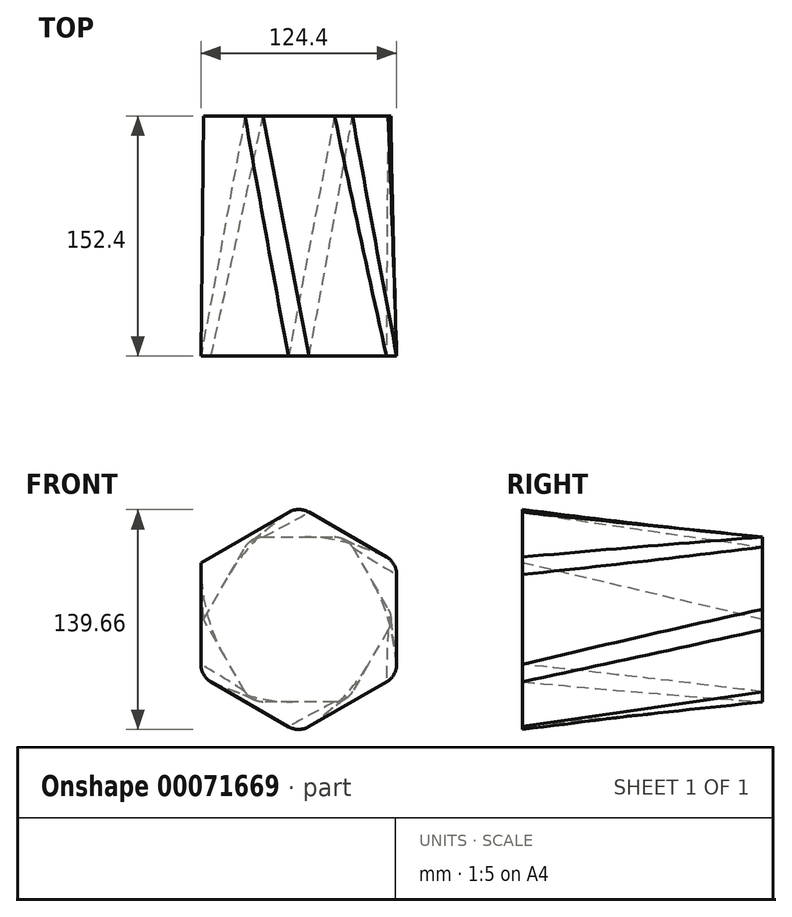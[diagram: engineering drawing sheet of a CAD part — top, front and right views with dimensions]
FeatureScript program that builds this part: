
annotation { "Feature Type Name" : "Feature", "Feature Type Description" : "" }
export const myFeature = defineFeature(function(context is Context, id is Id, definition is map)
    precondition{}
    {
        {
            var Q0;
            Q0=qCreatedBy(makeId("Front.planeOp"),FACE);
            var sketch = newSketch(context, id + "F0", { "sketchPlane" : qUnion([Q0])});
            skCircle(sketch, "E0.cCircle", {"center": v(0, 0) * mm, "radius": 52.46 * mm, "construction": true});
            skLineSegment(sketch, "E0.0", {"start": v(30.29, -52.46) * mm, "end": v(-30.29, -52.46) * mm});
            skLineSegment(sketch, "E0.1", {"start": v(-30.29, -52.46) * mm, "end": v(-60.57, 0) * mm});
            skLineSegment(sketch, "E0.2", {"start": v(-60.57, 0) * mm, "end": v(-30.29, 52.46) * mm});
            skLineSegment(sketch, "E0.3", {"start": v(-30.29, 52.46) * mm, "end": v(30.29, 52.46) * mm});
            skLineSegment(sketch, "E0.4", {"start": v(30.29, 52.46) * mm, "end": v(60.57, 0) * mm});
            skLineSegment(sketch, "E0.5", {"start": v(60.57, 0) * mm, "end": v(30.29, -52.46) * mm});
            skPoint(sketch, "E0.0.midPoint", {"position": v(0, -52.46) * mm});
            skSolve(sketch);
        }
        {
            var Q0;
            Q0=qCreatedBy(makeId("Front.planeOp"),FACE);
            cPlane(context, id + "F1", {"entities" : qUnion([Q0]), "cplaneType" : CPlaneType.OFFSET, "offset" : 152.4 * mm, "width" : 152.4 * mm, "height" : 152.4 * mm});
        }
        {
            var Q0;
            Q0=qCreatedBy(id+"F1.planeOp",FACE);
            var sketch = newSketch(context, id + "F2", { "sketchPlane" : qUnion([Q0])});
            skCircle(sketch, "E1.cCircle", {"center": v(0, 0) * mm, "radius": 62.2 * mm, "construction": true});
            skLineSegment(sketch, "E1.0", {"start": v(-62.2, -35.91) * mm, "end": v(-62.2, 35.91) * mm});
            skLineSegment(sketch, "E1.1", {"start": v(-62.2, 35.91) * mm, "end": v(0, 71.82) * mm});
            skLineSegment(sketch, "E1.2", {"start": v(0, 71.82) * mm, "end": v(62.2, 35.91) * mm});
            skLineSegment(sketch, "E1.3", {"start": v(62.2, 35.91) * mm, "end": v(62.2, -35.91) * mm});
            skLineSegment(sketch, "E1.4", {"start": v(62.2, -35.91) * mm, "end": v(0, -71.82) * mm});
            skLineSegment(sketch, "E1.5", {"start": v(0, -71.82) * mm, "end": v(-62.2, -35.91) * mm});
            skPoint(sketch, "E1.0.midPoint", {"position": v(-62.2, 0) * mm});
            skSolve(sketch);
        }
        {
            var Q0;
            Q0=makeQuery(id+"F0.imprint","IMPRINT",FACE,{"disambiguationData":[TD([[makeQuery(id+"F0.imprint","IMPRINT",EDGE,{"derivedFrom":sQuery(id+"F0.wireOp",EDGE,"E0.0")}),-1.0]])]});
            var Q1;
            Q1=makeQuery(id+"F2.imprint","IMPRINT",FACE,{"disambiguationData":[TD([[makeQuery(id+"F2.imprint","IMPRINT",EDGE,{"derivedFrom":sQuery(id+"F2.wireOp",EDGE,"E1.0")}),-1.0]])]});
            loft(context, id + "F3", {"sheetProfilesArray" : [{ "sheetProfileEntities" : qUnion([Q0]) }, { "sheetProfileEntities" : qUnion([Q1]) }]});
        }
        {
            var Q0;
            Q0=makeQuery(id+"F3.opLoft","SWEPT_EDGE",EDGE,{"disambiguationData":[OSD([sQuery(id+"F0.wireOp",EDGE,"E0.2"),sQuery(id+"F0.wireOp",EDGE,"E0.3"),sQuery(id+"F2.wireOp",EDGE,"E1.1"),sQuery(id+"F2.wireOp",EDGE,"E1.2")])]});
            var Q1;
            Q1=makeQuery(id+"F3.opLoft","SWEPT_EDGE",EDGE,{"disambiguationData":[OSD([sQuery(id+"F0.wireOp",EDGE,"E0.3"),sQuery(id+"F0.wireOp",EDGE,"E0.4"),sQuery(id+"F2.wireOp",EDGE,"E1.2"),sQuery(id+"F2.wireOp",EDGE,"E1.3")])]});
            var Q2;
            Q2=makeQuery(id+"F3.opLoft","SWEPT_EDGE",EDGE,{"disambiguationData":[OSD([sQuery(id+"F0.wireOp",EDGE,"E0.4"),sQuery(id+"F0.wireOp",EDGE,"E0.5"),sQuery(id+"F2.wireOp",EDGE,"E1.3"),sQuery(id+"F2.wireOp",EDGE,"E1.4")])]});
            var Q3;
            Q3=makeQuery(id+"F3.opLoft","SWEPT_EDGE",EDGE,{"disambiguationData":[OSD([sQuery(id+"F0.wireOp",EDGE,"E0.0"),sQuery(id+"F0.wireOp",EDGE,"E0.5"),sQuery(id+"F2.wireOp",EDGE,"E1.4"),sQuery(id+"F2.wireOp",EDGE,"E1.5")])]});
            var Q4;
            Q4=makeQuery(id+"F3.opLoft","SWEPT_EDGE",EDGE,{"disambiguationData":[OSD([sQuery(id+"F0.wireOp",EDGE,"E0.0"),sQuery(id+"F0.wireOp",EDGE,"E0.1"),sQuery(id+"F2.wireOp",EDGE,"E1.0"),sQuery(id+"F2.wireOp",EDGE,"E1.5")])]});
            fillet(context, id + "F4", {"entities" : qUnion([Q0, Q1, Q2, Q3, Q4]), "radius" : 12.7 * mm, "tangentPropagation" : true, "allowEdgeOverflow" : false});
        }
    });
